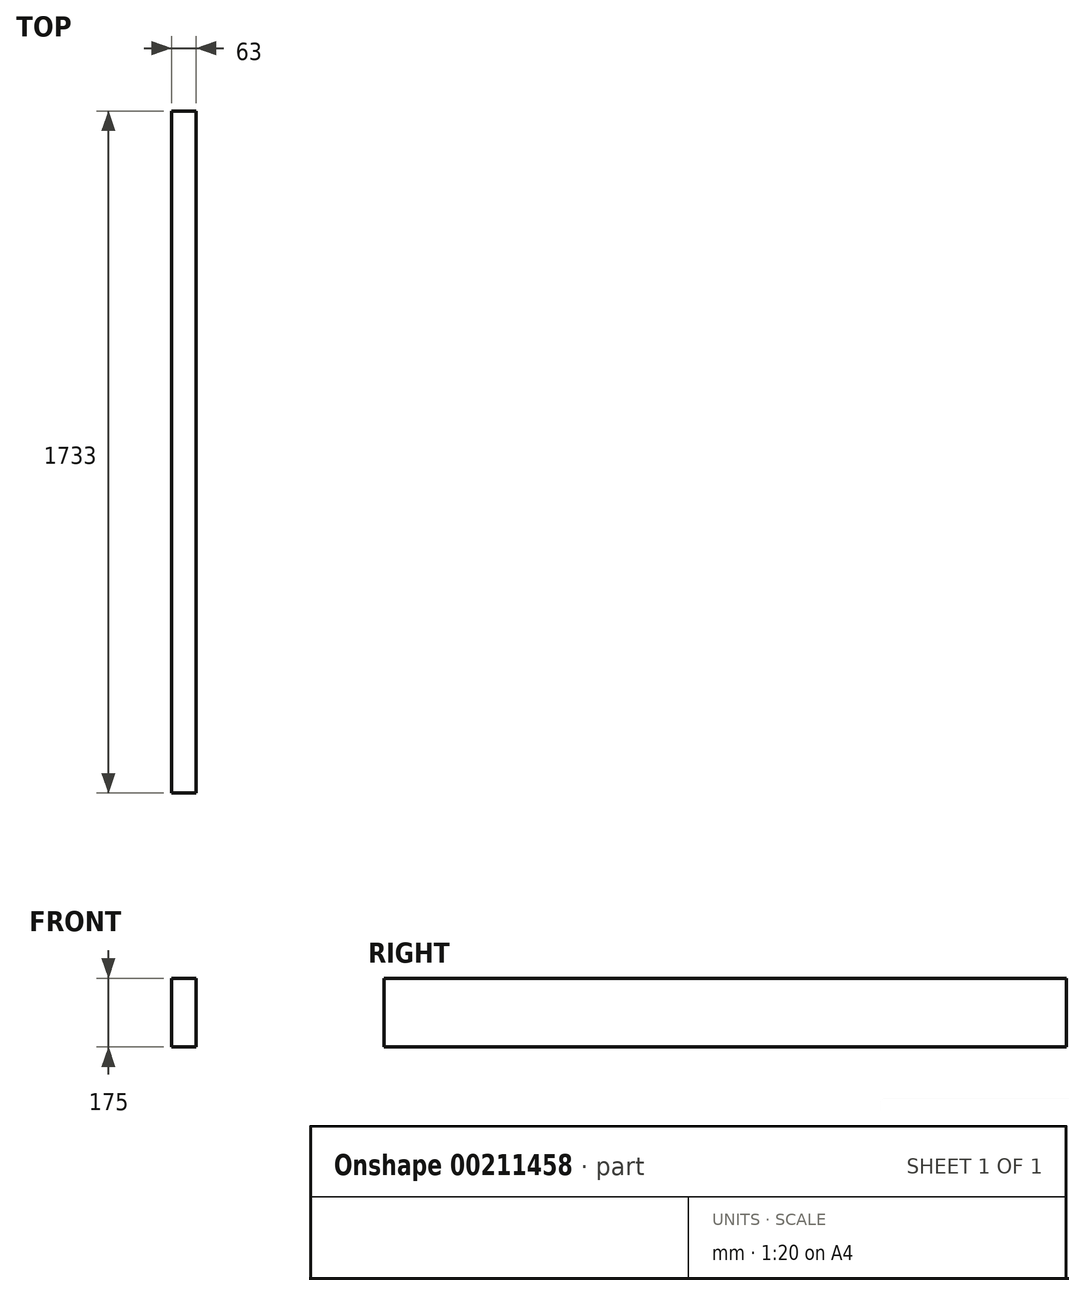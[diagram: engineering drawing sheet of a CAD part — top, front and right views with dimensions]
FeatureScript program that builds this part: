
annotation { "Feature Type Name" : "Feature", "Feature Type Description" : "" }
export const myFeature = defineFeature(function(context is Context, id is Id, definition is map)
    precondition{}
    {
        {
            var Q0;
            Q0=qCreatedBy(makeId("Front.planeOp"),FACE);
            var sketch = newSketch(context, id + "F0", { "sketchPlane" : qUnion([Q0])});
            skLineSegment(sketch, "E0.bottom", {"start": v(31.5, 87.5) * mm, "end": v(-31.5, 87.5) * mm});
            skLineSegment(sketch, "E0.top", {"start": v(31.5, -87.5) * mm, "end": v(-31.5, -87.5) * mm});
            skLineSegment(sketch, "E0.left", {"start": v(31.5, 87.5) * mm, "end": v(31.5, -87.5) * mm});
            skLineSegment(sketch, "E0.right", {"start": v(-31.5, 87.5) * mm, "end": v(-31.5, -87.5) * mm});
            skPoint(sketch, "E0.middle", {"position": v(0, 0) * mm});
            skSolve(sketch);
        }
        {
            var Q0;
            Q0=qSketchRegion(id+"F0",true);
            extrude(context, id + "F1", {"entities" : qUnion([Q0]), "depth" : (1450 + 323 - 40) * mm, "symmetric" : true});
        }
    });
